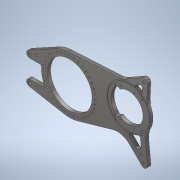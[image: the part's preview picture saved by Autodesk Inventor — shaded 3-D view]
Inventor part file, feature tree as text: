
AUTODESK INVENTOR PART (.ipt)
format: ipt  version: 2021 (Build 250183000, 183)  size: 591,872 bytes
history: native  units: in
note: dims shown in document units (in); Inventor stores cm internally (conversion verified against a paired STEP export)
features: sketch x19, extrude x13, hole x5, projected_geometry x3, chamfer x1, fillet x1
ambient origin geometry x8: Origin, YZ Plane, XZ Plane, XY Plane, X Axis, Y Axis, Z Axis, Center Point
bodies: Body1 (feature_tree)
feature tree (42):
  extrude  "Extrusion24"  Depth=2.16in
  extrude  "Extrusion28"  Depth=9.0in
  hole  "Hole9"  [1 undecoded]
  hole  "Hole11"  [1 undecoded]
  hole  "Hole13"  [1 undecoded]
  hole  "Hole14"  [1 undecoded]
  extrude  "Extrusion30"  Depth=0.5in
  extrude  "Extrusion31"  Depth=0.25in
  extrude  "Extrusion32"  Depth=7.75in
  extrude  "Extrusion33"  Depth=0.25in
  extrude  "Extrusion34"  Depth=1.0in
  chamfer  "Chamfer2"  Distance=5.0in
  extrude  "Extrusion35"  Depth=0.125in
  extrude  "Extrusion37"  Depth=0.125in TaperAngle=0.0deg
  extrude  "Extrusion39"  Depth=0.75in
  sketch  "Sketch58"  dims[d318=1.0in]
  hole  "Hole15"  [1 undecoded]
  extrude  "Extrusion40"  Depth=0.5in
  extrude  "Extrusion41"  Depth=0.75in
  fillet  "Fillet2"  Radius=0.75in
  extrude  "Extrusion42"  Depth=0.25in
  sketch  "Sketch2"  dims[d9=8.5in d92=2.16in]
  sketch  "Sketch35"  dims[d118=0.75in d119=0.75in d120=0.75in d121=0.75in d137=9.0in d142=6.5in]
  projected_geometry  "Projected Loop2"
  sketch  "Sketch36"  dims[d143=1.0in d210=1.0in]
  sketch  "Sketch40"  dims[d211=6.0in d212=6.0in]
  sketch  "Sketch43"  dims[d213=3.718in d214=1.0in]
  sketch  "Sketch45"  dims[d235=10.718in d237=1.5in]
  sketch  "Sketch46"  dims[d239=0.5in d240=0.0in d266=6.75in]
  sketch  "Sketch47"  dims[d267=0.5in d268=0.0in]
  sketch  "Sketch48"  dims[d269=0.386in d270=0.75in d271=0.762in d272=0.25in d273=0.5635in d274=0.484in d275=0.8108in d288=5.0in]
  sketch  "Sketch49"  dims[d289=17.223in d290=7.75in]
  sketch  "Sketch50"  dims[d291=3.5433in d293=360.0deg]
  sketch  "Sketch53"  dims[d295=0.257in d296=0.75in d297=0.438in d298=0.25in d299=0.5635in d300=1.0in d301=0.8108in d302=0.1718in]
  sketch  "Sketch55"  dims[d303=15.0deg d316=1.0in]
  sketch  "Sketch57"  dims[d317=0.0481in]
  sketch  "Sketch59"  dims[d319=0.3972in]
  sketch  "Sketch60"  dims[d322=0.271in]
  sketch  "Sketch62"  dims[d323=0.1355in]
  sketch  "Sketch63"  dims[d324=0.5in d325=0.266in d326=0.75in d327=0.507in d328=0.25in d329=0.5635in d330=1.0in d331=0.8108in d332=0.5in d333=0.5in d334=0.5in d335=0.5in d336=0.5in d337=3.0in d338=5.0in d339=0.196in d340=0.5in d341=0.507in d342=0.25in d343=0.5635in d344=0.75in d345=0.0in d346=3.0in d347=1.0in d348=0.0in d349=0.75in d350=0.75in d351=0.5in d353=0.75in d354=0.75in d355=0.25in d356=1.0in d357=0.0in d358=0.25in d359=1.0in d360=0.0in d361=1.0in d362=1.0in d363=0.25in d364=1.0in d365=0.0in d366=2.5in d367=1.0in d368=0.0in d373=0.0156in d374=0.125in d375=45.0deg d376=6.65in d377=6.25in d378=0.075in d379=0.0in d381=1.1915in d382=2.3407in d383=0.878in d384=2.3407in d395=0.5in d396=0.5in d397=1.0in d398=0.0in d403=1.0in d404=0.0in d405=0.5in d406=0.5in d407=2.01in d408=2.01in d409=2.01in d410=2.01in d411=2.01in d412=2.01in d413=2.01in d414=2.01in d415=0.196in d416=0.5in d417=0.375in d418=0.25in d419=0.5635in d420=1.0in d421=0.8108in d422=6.029in d423=6.63in d424=0.075in d425=0.0in d429=0.3369in d430=0.878in d431=2.1978in d432=1.0in d433=0.0in d434=0.125in d435=1.0in d436=0.0in]
  projected_geometry  "Project Cut Edges2"
  projected_geometry  "Project Cut Edges4"
note: 5 required parameter values undecoded (feature->parameter linkage not recoverable at this tier; creation-order binding heuristic only, values carry confidence <= 0.55)
